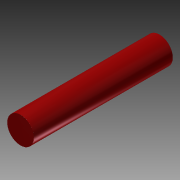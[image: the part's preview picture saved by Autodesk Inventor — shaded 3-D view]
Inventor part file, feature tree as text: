
AUTODESK INVENTOR PART (.ipt)
format: ipt  version: 2013 (Build 170138000, 138)  size: 103,424 bytes
history: native  units: mm
features: sketch x6, extrude x5, other x1, hole x1
ambient origin geometry x8: Origin, YZ Plane, XZ Plane, XY Plane, X Axis, Y Axis, Z Axis, Center Point
feature tree (13):
  other  "ソリッド1"
  extrude  "押し出し1"  Depth=14.0mm
  sketch  "スケッチ2"
  extrude  "押し出し2"  Depth=70.0mm TaperAngle=0.0deg
  extrude  "押し出し3"  Depth=55.0mm
  hole  "穴1"  [1 undecoded]
  extrude  "押し出し5"  Depth=3.0mm TaperAngle=0.0deg
  extrude  "押し出し6"  Depth=50.0mm
  sketch  "スケッチ1"
  sketch  "スケッチ3"
  sketch  "スケッチ4"
  sketch  "スケッチ6"
  sketch  "スケッチ7"
note: 1 required parameter value undecoded (feature->parameter linkage not recoverable at this tier; creation-order binding heuristic only, values carry confidence <= 0.55)
